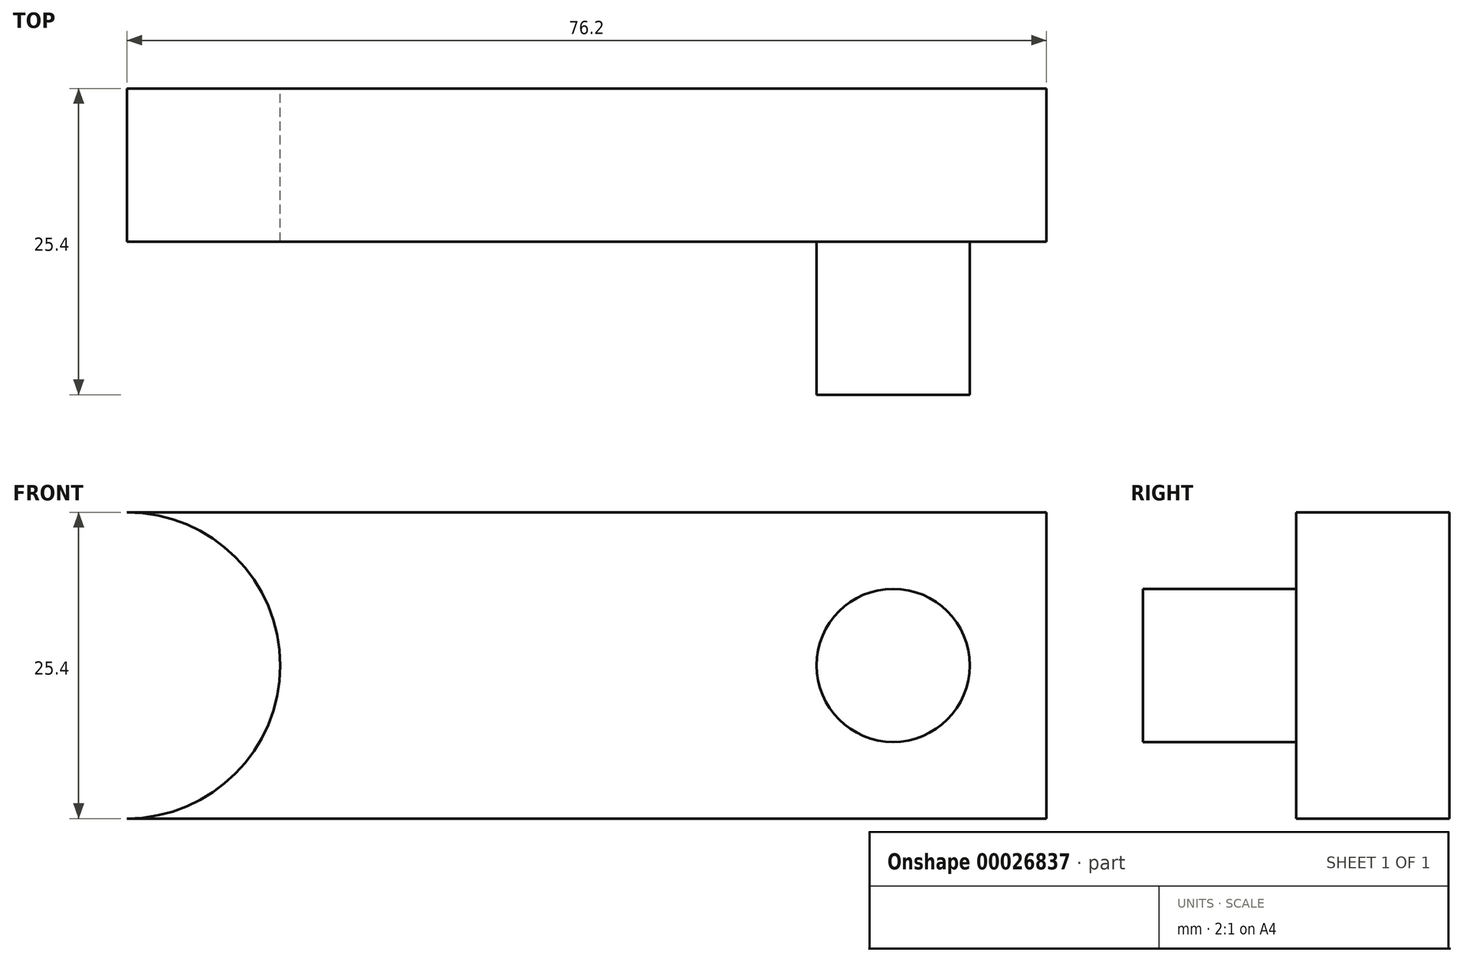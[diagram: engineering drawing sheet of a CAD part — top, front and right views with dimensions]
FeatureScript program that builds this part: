
annotation { "Feature Type Name" : "Feature", "Feature Type Description" : "" }
export const myFeature = defineFeature(function(context is Context, id is Id, definition is map)
    precondition{}
    {
        {
            var Q0;
            Q0=qCreatedBy(makeId("Front.planeOp"),FACE);
            var sketch = newSketch(context, id + "F0", { "sketchPlane" : qUnion([Q0])});
            skLineSegment(sketch, "E0.bottom", {"start": v(0, 0) * mm, "end": v(76.2, 0) * mm});
            skLineSegment(sketch, "E0.top", {"start": v(0, 25.4) * mm, "end": v(76.2, 25.4) * mm});
            skLineSegment(sketch, "E0.right", {"start": v(76.2, 0) * mm, "end": v(76.2, 25.4) * mm});
            skPoint(sketch, "E1", {"position": v(0, 12.7) * mm});
            skArc(sketch, "E2", {"start": v(0, 0) * mm, "mid": v(12.7, 12.7) * mm, "end": v(0, 25.4) * mm});
            skPoint(sketch, "E3", {"position": v(76.2, 12.7) * mm});
            skPoint(sketch, "E4", {"position": v(63.5, 12.7) * mm});
            skCircle(sketch, "E5", {"center": v(63.5, 12.7) * mm, "radius": 6.35 * mm});
            skSolve(sketch);
        }
        {
            var Q0;
            Q0=makeQuery(id+"F0.imprint","IMPRINT",FACE,{"disambiguationData":[TD([[makeQuery(id+"F0.imprint","IMPRINT",EDGE,{"derivedFrom":sQuery(id+"F0.wireOp",EDGE,"E0.bottom")}),1.0]])]});
            extrude(context, id + "F1", {"entities" : qUnion([Q0]), "depth" : 12.7 * mm});
        }
        {
            var Q0;
            Q0=makeQuery(id+"F0.imprint","IMPRINT",FACE,{"disambiguationData":[TD([[makeQuery(id+"F0.imprint","IMPRINT",EDGE,{"derivedFrom":sQuery(id+"F0.wireOp",EDGE,"E5")}),1.0]])]});
            extrude(context, id + "F2", {"entities" : qUnion([Q0]), "operationType" : NewBodyOperationType.ADD, "depth" : 25.4 * mm});
        }
    });
